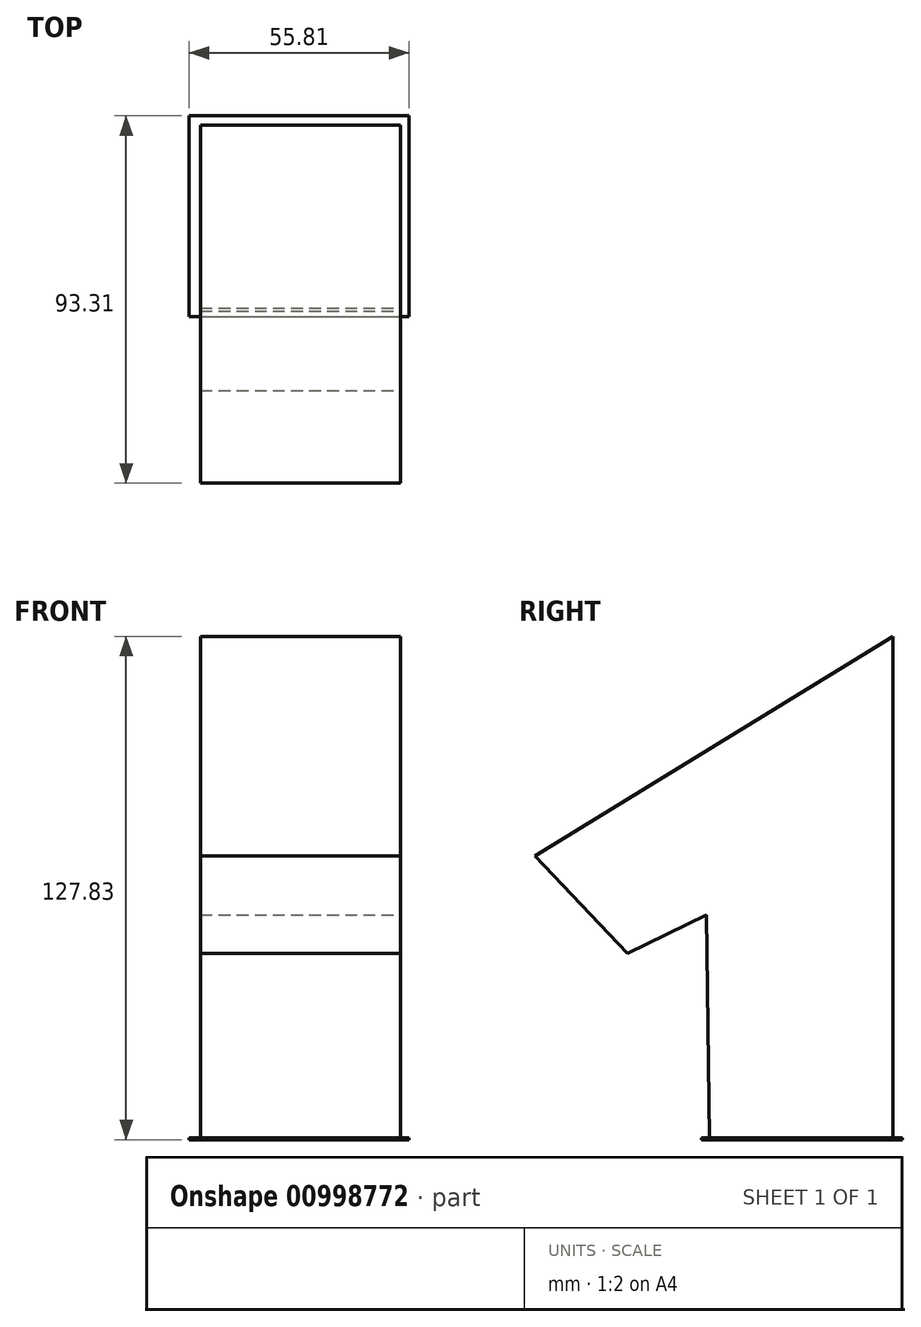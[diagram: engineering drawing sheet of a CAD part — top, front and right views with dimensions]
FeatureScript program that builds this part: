
annotation { "Feature Type Name" : "Feature", "Feature Type Description" : "" }
export const myFeature = defineFeature(function(context is Context, id is Id, definition is map)
    precondition{}
    {
        {
            var Q0;
            Q0=qCreatedBy(makeId("Right.planeOp"),FACE);
            var sketch = newSketch(context, id + "F0", { "sketchPlane" : qUnion([Q0])});
            skLineSegment(sketch, "E0", {"start": v(-22.79, 0) * mm, "end": v(23.73, 0) * mm});
            skLineSegment(sketch, "E1", {"start": v(23.73, 0) * mm, "end": v(23.73, 127.32) * mm});
            skLineSegment(sketch, "E2", {"start": v(23.73, 127.32) * mm, "end": v(-67.18, 71.63) * mm});
            skLineSegment(sketch, "E3", {"start": v(-23.54, 56.62) * mm, "end": v(-22.79, 0) * mm});
            skLineSegment(sketch, "E4", {"start": v(-23.54, 56.62) * mm, "end": v(-43.72, 46.76) * mm});
            skLineSegment(sketch, "E5", {"start": v(-67.18, 71.63) * mm, "end": v(-43.72, 46.76) * mm});
            skSolve(sketch);
        }
        {
            var Q0;
            Q0=makeQuery(id+"F0.imprint","IMPRINT",FACE,{"disambiguationData":[TD([[makeQuery(id+"F0.imprint","IMPRINT",EDGE,{"derivedFrom":sQuery(id+"F0.wireOp",EDGE,"E0")}),1.0]])]});
            extrude(context, id + "F1", {"entities" : qUnion([Q0]), "oppositeDirection" : true, "depth" : 50.8 * mm, "offsetDistance" : 25.4 * mm});
        }
        {
            var Q0;
            Q0=qCreatedBy(makeId("Top.planeOp"),FACE);
            var sketch = newSketch(context, id + "F2", { "sketchPlane" : qUnion([Q0])});
            skLineSegment(sketch, "E6.bottom", {"start": v(-53.66, 26.13) * mm, "end": v(2.15, 26.13) * mm});
            skLineSegment(sketch, "E6.top", {"start": v(-53.66, -24.86) * mm, "end": v(2.15, -24.86) * mm});
            skLineSegment(sketch, "E6.left", {"start": v(-53.66, 26.13) * mm, "end": v(-53.66, -24.86) * mm});
            skLineSegment(sketch, "E6.right", {"start": v(2.15, 26.13) * mm, "end": v(2.15, -24.86) * mm});
            skPoint(sketch, "E6.middle", {"position": v(-25.75, 0.63) * mm});
            skSolve(sketch);
        }
        {
            var Q0;
            Q0=makeQuery(id+"F2.imprint","IMPRINT",FACE,{"disambiguationData":[TD([[makeQuery(id+"F2.imprint","IMPRINT",EDGE,{"derivedFrom":sQuery(id+"F2.wireOp",EDGE,"E6.bottom")}),-1.0]])]});
            extrude(context, id + "F3", {"entities" : qUnion([Q0]), "operationType" : NewBodyOperationType.ADD, "oppositeDirection" : true, "depth" : 0.5 * mm, "offsetDistance" : 25.4 * mm});
        }
    });
